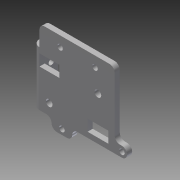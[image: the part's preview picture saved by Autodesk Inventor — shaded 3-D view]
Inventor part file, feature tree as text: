
AUTODESK INVENTOR PART (.ipt)
format: ipt  version: 2013 (Build 170138000, 138)  size: 280,576 bytes
history: native  units: in
note: dims shown in document units (in); Inventor stores cm internally (conversion verified against a paired STEP export)
features: sheet_metal_op x6, other x6, sketch x5, chamfer x1
ambient origin geometry x8: Origin, YZ Plane, XZ Plane, XY Plane, X Axis, Y Axis, Z Axis, Center Point
bodies: Solid1 (feature_tree)
feature tree (18):
  sheet_metal_op  "Face1"
  sheet_metal_op  "Flange1"
  sheet_metal_op  "Face2"
  chamfer  "Corner Round1"
  sketch  "Sketch1"  dims[d0=0.5625in]
  other  "Plate1"
  sketch  "Sketch2"  dims[d1=0.5in]
  other  "Plate2"
  sheet_metal_op  "Bend1"
  sheet_metal_op  "Corner1"
  sketch  "Sketch3"  dims[d2=0.5in]
  sketch  "Sketch4"  dims[d3=1.0in]
  other  "Plate3"
  sheet_metal_op  "Bend2"
  sketch  "Sketch5"  dims[d4=0.25in d5=0.266in d11=0.25in d16=0.25in d23=0.6in d24=0.5in d25=0.35in d26=0.266in d27=0.25in d28=0.125in d29=0.5in d30=0.25in d31=1.0in d32=90.0deg d33=0.0965in d34=1.0in d35=0.25in d36=0.25in d37=1.0in d38=1.0in d39=0.266in d40=0.266in d41=0.25in d42=0.0in d43=1.0in d44=1.0in d45=1.0in d47=0.266in d48=0.0in d49=0.25in d50=0.25in d51=0.125in d52=0.5in d53=0.25in d54=0.266in d55=0.25in d56=0.0in d57=0.25in]
  other  "Cut1"
  other  "Cut2"
  other  "Definition1"
